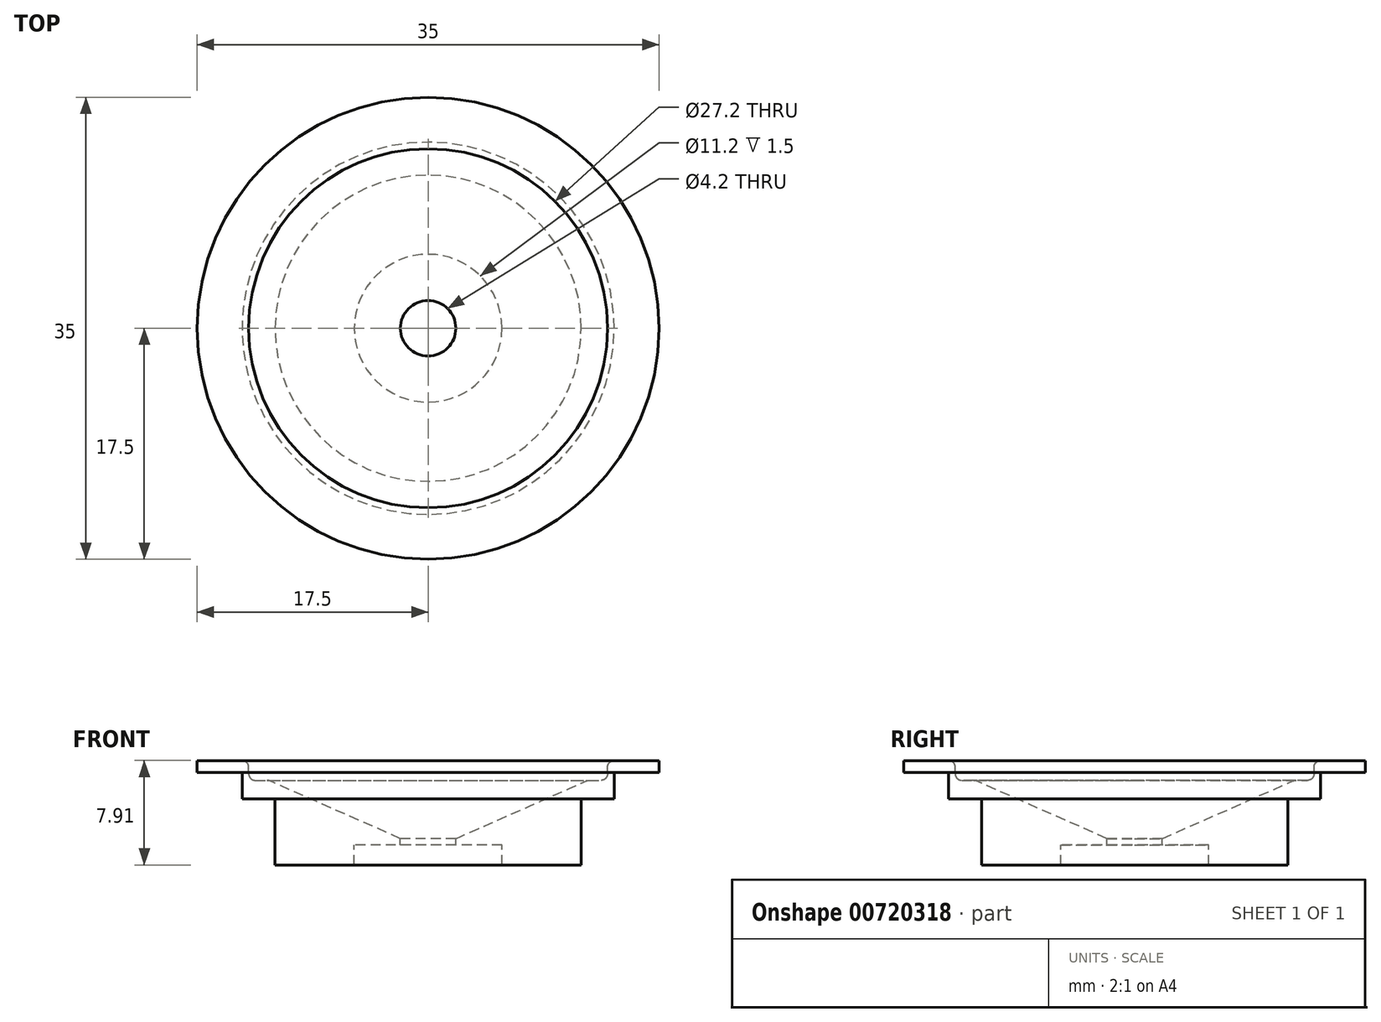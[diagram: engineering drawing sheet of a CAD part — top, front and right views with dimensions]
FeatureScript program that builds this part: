
annotation { "Feature Type Name" : "Feature", "Feature Type Description" : "" }
export const myFeature = defineFeature(function(context is Context, id is Id, definition is map)
    precondition{}
    {
        {
            var Q0;
            Q0=qCreatedBy(makeId("Front.planeOp"),FACE);
            var sketch = newSketch(context, id + "F0", { "sketchPlane" : qUnion([Q0])});
            skLineSegment(sketch, "E0", {"start": v(0, 0) * mm, "end": v(-11.6, 0) * mm});
            skLineSegment(sketch, "E1", {"start": v(-11.6, 0) * mm, "end": v(-14.1, 0) * mm});
            skLineSegment(sketch, "E2", {"start": v(-14.1, 0) * mm, "end": v(-14.1, 2) * mm});
            skLineSegment(sketch, "E3", {"start": v(-14.1, 2) * mm, "end": v(-17.5, 2) * mm});
            skLineSegment(sketch, "E4", {"start": v(0, 0) * mm, "end": v(0, -15) * mm});
            skLineSegment(sketch, "E5", {"start": v(-11.6, 0) * mm, "end": v(-11.6, -5) * mm});
            skLineSegment(sketch, "E6", {"start": v(-11.6, -5) * mm, "end": v(-5.6, -5) * mm});
            skLineSegment(sketch, "E7", {"start": v(-5.6, -5) * mm, "end": v(-5.6, -3.5) * mm});
            skLineSegment(sketch, "E8", {"start": v(-5.6, -3.5) * mm, "end": v(-2.1, -3.5) * mm});
            skLineSegment(sketch, "E9", {"start": v(-17.5, 2) * mm, "end": v(-17.5, 2.9) * mm});
            skLineSegment(sketch, "E10", {"start": v(-2.1, -3.5) * mm, "end": v(-2.1, -3) * mm});
            skLineSegment(sketch, "E11", {"start": v(-17.5, 2.9) * mm, "end": v(-13.6, 2.9) * mm});
            skLineSegment(sketch, "E12", {"start": v(-13.6, 2.9) * mm, "end": v(-13.6, 1.4) * mm});
            skLineSegment(sketch, "E13", {"start": v(-13.6, 1.4) * mm, "end": v(-12.1, 1.4) * mm});
            skLineSegment(sketch, "E14", {"start": v(-12.1, 1.4) * mm, "end": v(-2.1, -3) * mm});
            skSolve(sketch);
        }
        {
            var Q0;
            {var subQ0=sQuery(id+"F0.wireOp",EDGE,"E5");Q0=makeQuery(id+"F0.imprint","IMPRINT",FACE,{"disambiguationData":[TD([[makeQuery(id+"F0.imprint","IMPRINT",EDGE,{"derivedFrom":subQ0}),1.0]])]});}
            var Q1;
            {var subQ0=sQuery(id+"F0.wireOp",EDGE,"E1");Q1=makeQuery(id+"F0.imprint","IMPRINT",FACE,{"disambiguationData":[TD([[makeQuery(id+"F0.imprint","IMPRINT",EDGE,{"derivedFrom":subQ0}),-1.0]])]});}
            var Q2;
            Q2=sQuery(id+"F0.wireOp",EDGE,"E4");
            revolve(context, id + "F1", {"surfaceOperationType" : NewSurfaceOperationType.NEW, "entities" : qUnion([Q0, Q1]), "axis" : qUnion([Q2]), "revolveType" : RevolveType.FULL});
        }
        {
            var Q0;
            Q0=makeQuery(id+"F1.opRevolve","SWEPT_FACE",FACE,{"disambiguationData":[OSD([sQuery(id+"F0.wireOp",EDGE,"E11")])]});
            var sketch = newSketch(context, id + "F2", { "sketchPlane" : qUnion([Q0])});
            skSolve(sketch);
        }
        {
            var Q0;
            Q0=makeQuery(id+"F2.imprint","IMPRINT",FACE,{"disambiguationData":[TD([[makeQuery(id+"F2.imprint","IMPRINT",EDGE,{"derivedFrom":makeQuery(id+"F1.opRevolve","SWEPT_EDGE",EDGE,{"disambiguationData":[OSD([sQuery(id+"F0.wireOp",EDGE,"E11"),sQuery(id+"F0.wireOp",EDGE,"KBah7Gp4-EKzU-XpPn-CMNs-DqB0rEozPnCd")])]})}),1.0]])]});
            extrude(context, id + "F3", {"entities" : qUnion([Q0]), "operationType" : NewBodyOperationType.REMOVE, "oppositeDirection" : true, "depth" : 1.5 * mm, "offsetDistance" : 25 * mm});
        }
        {
            var Q0;
            Q0=makeQuery(id+"F1.opRevolve","SWEPT_EDGE",EDGE,{"disambiguationData":[OSD([sQuery(id+"F0.wireOp",EDGE,"E12"),sQuery(id+"F0.wireOp",EDGE,"E13")])]});
            fillet(context, id + "F4", {"entities" : qUnion([Q0]), "tangentPropagation" : true, "radius" : 0.5 * mm, "defaultsChanged" : true, "vertexSettings" : [], "allowEdgeOverflow" : false});
        }
        {
            var Q0;
            Q0=makeQuery(id+"F1.opRevolve","SWEPT_EDGE",EDGE,{"disambiguationData":[OSD([sQuery(id+"F0.wireOp",EDGE,"E13"),sQuery(id+"F0.wireOp",EDGE,"E14")])]});
            fillet(context, id + "F5", {"entities" : qUnion([Q0]), "tangentPropagation" : true, "radius" : 0.5 * mm, "defaultsChanged" : true, "vertexSettings" : [], "allowEdgeOverflow" : false});
        }
        {
            var Q0;
            Q0=makeQuery(id+"F1.opRevolve","SWEPT_EDGE",EDGE,{"disambiguationData":[OSD([sQuery(id+"F0.wireOp",EDGE,"E11"),sQuery(id+"F0.wireOp",EDGE,"E12")])]});
            fillet(context, id + "F6", {"entities" : qUnion([Q0]), "tangentPropagation" : true, "radius" : 0.5 * mm, "defaultsChanged" : true, "vertexSettings" : [], "allowEdgeOverflow" : false});
        }
    });
